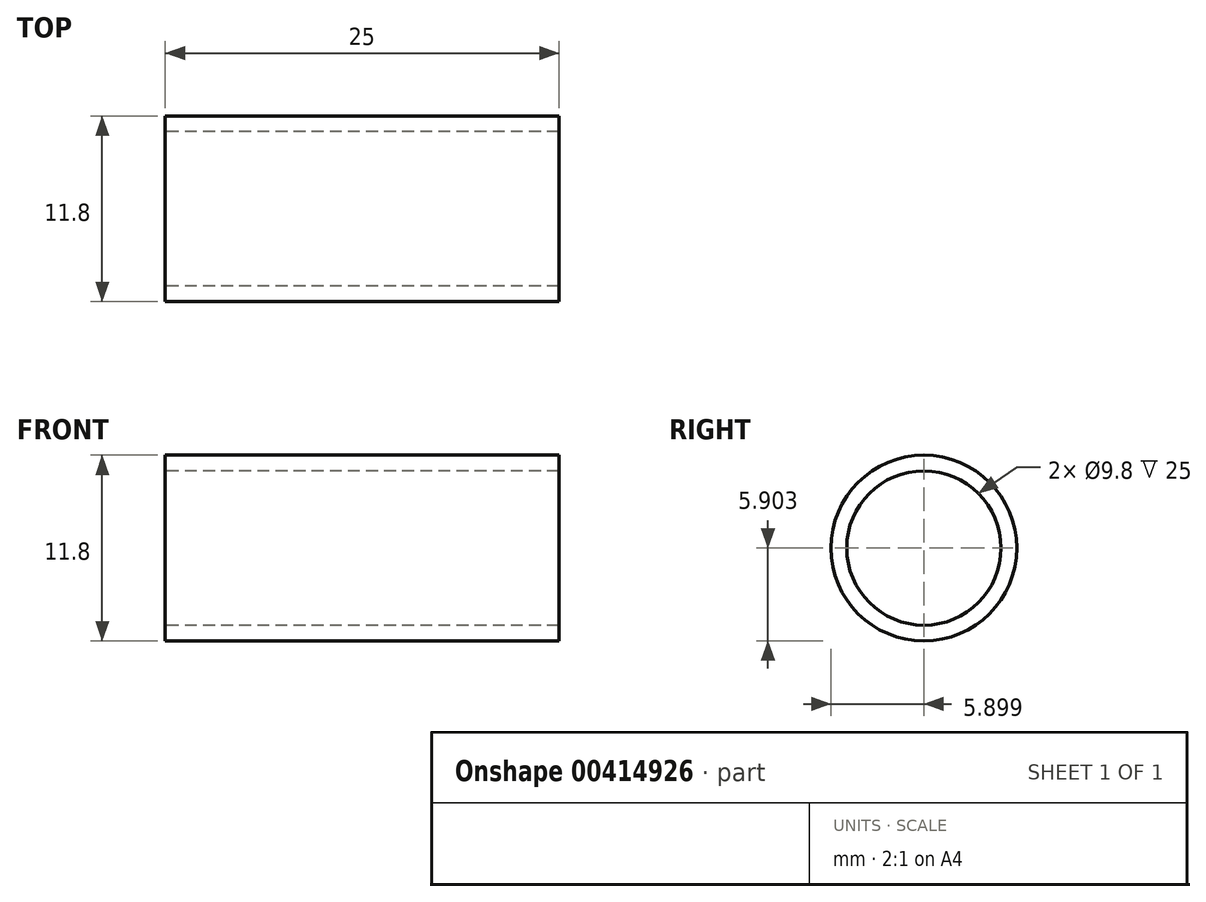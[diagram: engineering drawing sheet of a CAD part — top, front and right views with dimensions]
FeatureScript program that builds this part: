
annotation { "Feature Type Name" : "Feature", "Feature Type Description" : "" }
export const myFeature = defineFeature(function(context is Context, id is Id, definition is map)
    precondition{}
    {
        {
            var Q0;
            Q0=qCreatedBy(makeId("Right.planeOp"),FACE);
            var sketch = newSketch(context, id + "F0", { "sketchPlane" : qUnion([Q0])});
            skCircle(sketch, "E0", {"center": v(-4.55, 12.7) * mm, "radius": 5.9 * mm});
            skCircle(sketch, "E1", {"center": v(-4.55, 12.7) * mm, "radius": 4.9 * mm});
            skSolve(sketch);
        }
        {
            var Q0;
            Q0 = qSketchRegion(id + "F0", true);
            extrude(context, id + "F1", {"entities" : qUnion([Q0]), "depth" : 25 * mm});
        }
    });
